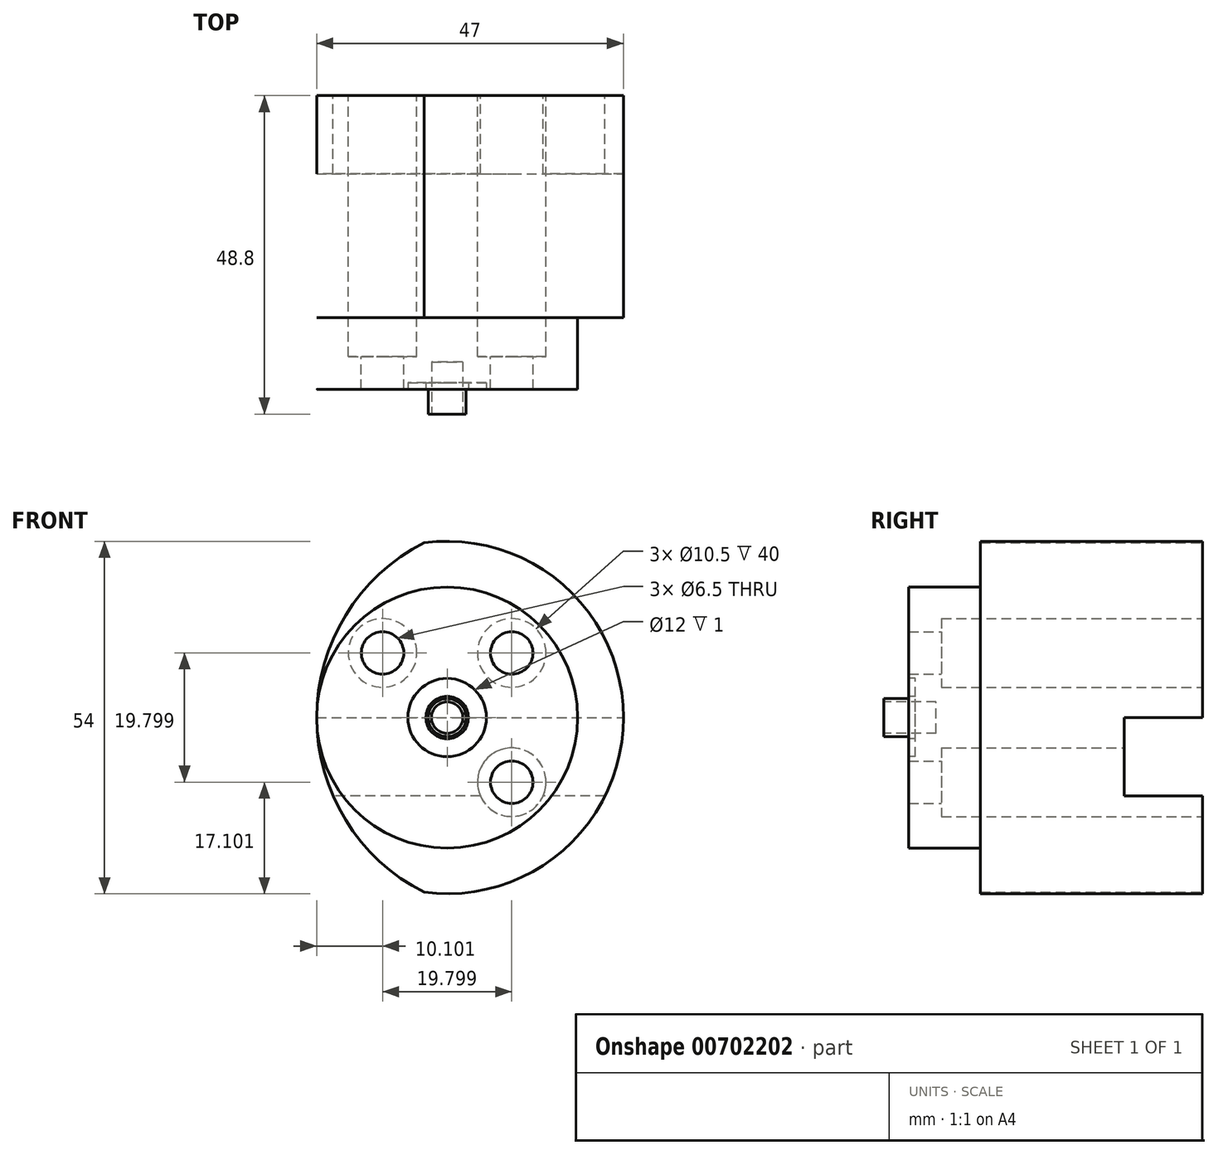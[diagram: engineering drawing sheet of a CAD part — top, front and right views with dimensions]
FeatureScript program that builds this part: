
annotation { "Feature Type Name" : "Feature", "Feature Type Description" : "" }
export const myFeature = defineFeature(function(context is Context, id is Id, definition is map)
    precondition{}
    {
        {
            var Q0;
            Q0=qCreatedBy(makeId("Front.planeOp"),FACE);
            var sketch = newSketch(context, id + "F0", { "sketchPlane" : qUnion([Q0])});
            skCircle(sketch, "E0", {"center": v(0, 0) * mm, "radius": 27 * mm});
            skSolve(sketch);
        }
        {
            var Q0;
            Q0 = qSketchRegion(id + "F0", true);
            extrude(context, id + "F1", {"entities" : qUnion([Q0]), "depth" : 45 * mm, "offsetDistance" : 25 * mm});
        }
        {
            var Q0;
            Q0=makeQuery(id+"F1.opExtrude","CAP_FACE",FACE,{"disambiguationData":[OSD([sQuery(id+"F0.wireOp",EDGE,"E0")])],"isStart":false});
            var sketch = newSketch(context, id + "F2", { "sketchPlane" : qUnion([Q0])});
            skCircle(sketch, "E1", {"center": v(0, 0) * mm, "radius": 20 * mm});
            skCircle(sketch, "E2", {"center": v(0, 0) * mm, "radius": 41.84 * mm});
            skSolve(sketch);
        }
        {
            var Q0;
            Q0 = qSketchRegion(id + "F2", true);
            extrude(context, id + "F3", {"entities" : qUnion([Q0]), "operationType" : NewBodyOperationType.REMOVE, "oppositeDirection" : true, "depth" : 11 * mm, "offsetDistance" : 25 * mm});
        }
        {
            var Q0;
            Q0=makeQuery(id+"F1.opExtrude","CAP_FACE",FACE,{"disambiguationData":[OSD([sQuery(id+"F0.wireOp",EDGE,"E0")])],"isStart":true});
            var sketch = newSketch(context, id + "F4", { "sketchPlane" : qUnion([Q0])});
            skPoint(sketch, "E3", {"position": v(9.9, 9.9) * mm});
            skLineSegment(sketch, "E4", {"start": v(9.9, 9.9) * mm, "end": v(0, 0) * mm});
            skLineSegment(sketch, "E5", {"start": v(0, 0) * mm, "end": v(47.47, 0) * mm});
            skLineSegment(sketch, "E6", {"start": v(0, 0) * mm, "end": v(0, 46.24) * mm});
            skPoint(sketch, "E7.MirrorP", {"position": v(-9.9, 9.9) * mm});
            skPoint(sketch, "E8.MirrorP", {"position": v(-9.9, -9.9) * mm});
            skSolve(sketch);
        }
        {
            var Q0;
            Q0=sQuery(id+"F4.wireOp",VERTEX,"E7.MirrorP");
            var Q1;
            Q1=sQuery(id+"F4.wireOp",VERTEX,"E3");
            var Q2;
            Q2=sQuery(id+"F4.wireOp",VERTEX,"42431aa4-3257-4c28-8b8a-731fc5cc6f3b0.MirrorP");
            var Q3;
            Q3=sQuery(id+"F4.wireOp",VERTEX,"E8.MirrorP");
            var Q4;
            Q4=makeQuery(id+"F1.opExtrude","SWEPT_BODY",BODY,{"disambiguationData":[OSD([sQuery(id+"F0.wireOp",EDGE,"E0")])]});
            hole(context, id + "F5", {"style" : HoleStyle.SIMPLE, "endStyle" : HoleEndStyle.BLIND, "holeDiameter" : 6.5 * mm, "majorDiameter" : 5 * mm, "holeDepth" : 50 * mm, "isTappedThrough" : true, "tappedDepth" : 12 * mm, "tapClearance" : 3, "locations" : qUnion([Q0, Q1, Q2, Q3]), "scope" : qUnion([Q4])});
        }
        {
            var Q0;
            Q0=makeQuery(id+"F1.opExtrude","CAP_FACE",FACE,{"disambiguationData":[OSD([sQuery(id+"F0.wireOp",EDGE,"E0")])],"isStart":true});
            var sketch = newSketch(context, id + "F6", { "sketchPlane" : qUnion([Q0])});
            skCircle(sketch, "E9", {"center": v(-9.9, -9.9) * mm, "radius": 5.25 * mm});
            skCircle(sketch, "E10", {"center": v(9.9, 9.9) * mm, "radius": 5.25 * mm});
            skCircle(sketch, "E11", {"center": v(-9.9, 9.9) * mm, "radius": 5.25 * mm});
            skSolve(sketch);
        }
        {
            var Q0;
            Q0 = qSketchRegion(id + "F6", true);
            extrude(context, id + "F7", {"entities" : qUnion([Q0]), "operationType" : NewBodyOperationType.REMOVE, "oppositeDirection" : true, "depth" : 40 * mm, "offsetDistance" : 25 * mm});
        }
        {
            var Q0;
            Q0=makeQuery(id+"F1.opExtrude","CAP_FACE",FACE,{"disambiguationData":[OSD([sQuery(id+"F0.wireOp",EDGE,"E0")])],"isStart":false});
            var sketch = newSketch(context, id + "F8", { "sketchPlane" : qUnion([Q0])});
            skCircle(sketch, "E12", {"center": v(0, 0) * mm, "radius": 2.9 * mm});
            skSolve(sketch);
        }
        {
            var Q0;
            Q0 = qSketchRegion(id + "F8", true);
            extrude(context, id + "F9", {"entities" : qUnion([Q0]), "operationType" : NewBodyOperationType.ADD, "depth" : 3.8 * mm, "offsetDistance" : 25 * mm});
        }
        {
            var Q0;
            Q0=makeQuery(id+"F9.opExtrude","CAP_FACE",FACE,{"disambiguationData":[OSD([sQuery(id+"F8.wireOp",EDGE,"E12")])],"isStart":false});
            var sketch = newSketch(context, id + "F10", { "sketchPlane" : qUnion([Q0])});
            skCircle(sketch, "E13", {"center": v(0, 0) * mm, "radius": 2.4 * mm});
            skSolve(sketch);
        }
        {
            var Q0;
            Q0 = qSketchRegion(id + "F10", true);
            extrude(context, id + "F11", {"entities" : qUnion([Q0]), "operationType" : NewBodyOperationType.REMOVE, "oppositeDirection" : true, "depth" : 8 * mm, "offsetDistance" : 25 * mm});
        }
        {
            var Q0;
            Q0=makeQuery(id+"F1.opExtrude","CAP_FACE",FACE,{"disambiguationData":[OSD([sQuery(id+"F0.wireOp",EDGE,"E0")])],"isStart":false});
            var sketch = newSketch(context, id + "F12", { "sketchPlane" : qUnion([Q0])});
            skCircle(sketch, "E14", {"center": v(0, 0) * mm, "radius": 6 * mm});
            skCircle(sketch, "E15", {"center": v(0, 0) * mm, "radius": 3.25 * mm});
            skSolve(sketch);
        }
        {
            var Q0;
            Q0 = qSketchRegion(id + "F12", true);
            extrude(context, id + "F13", {"entities" : qUnion([Q0]), "operationType" : NewBodyOperationType.REMOVE, "oppositeDirection" : true, "depth" : 1 * mm, "offsetDistance" : 25 * mm});
        }
        {
            var Q0;
            Q0=makeQuery(id+"F1.opExtrude","CAP_FACE",FACE,{"disambiguationData":[OSD([sQuery(id+"F0.wireOp",EDGE,"E0")])],"isStart":true});
            var sketch = newSketch(context, id + "F14", { "sketchPlane" : qUnion([Q0])});
            skLineSegment(sketch, "E16", {"start": v(0, 0) * mm, "end": v(-37.34, 0) * mm});
            skLineSegment(sketch, "E17", {"start": v(-37.34, 0) * mm, "end": v(-37.34, -12) * mm});
            skLineSegment(sketch, "E18", {"start": v(-37.34, -12) * mm, "end": v(41.68, -12) * mm});
            skLineSegment(sketch, "E19", {"start": v(41.68, -12) * mm, "end": v(39.8, 0) * mm});
            skLineSegment(sketch, "E20", {"start": v(39.8, 0) * mm, "end": v(0, 0) * mm});
            skSolve(sketch);
        }
        {
            var Q0;
            Q0 = qSketchRegion(id + "F14", true);
            extrude(context, id + "F15", {"entities" : qUnion([Q0]), "operationType" : NewBodyOperationType.REMOVE, "oppositeDirection" : true, "depth" : 12 * mm, "offsetDistance" : 25 * mm});
        }
        {
            var Q0;
            {var subQ0=sQuery(id+"F0.wireOp",EDGE,"E0");Q0=makeQuery(id+"F15.boolean.opBoolean","SPLIT",FACE,{"disambiguationData":[TD([makeQuery(id+"F7.boolean.opBoolean","COPY",FACE,{"derivedFrom":makeQuery(id+"F7.opExtrude","SWEPT_FACE",FACE,{"disambiguationData":[OSD([sQuery(id+"F6.wireOp",EDGE,"E10")])]})})])],"derivedFrom":makeQuery(id+"F1.opExtrude","CAP_FACE",FACE,{"disambiguationData":[OSD([subQ0])],"isStart":true})});}
            var sketch = newSketch(context, id + "F16", { "sketchPlane" : qUnion([Q0])});
            skPoint(sketch, "E21", {"position": v(20, 0) * mm});
            skPoint(sketch, "E22", {"position": v(27, 0) * mm});
            skPoint(sketch, "E23", {"position": v(-10, 0) * mm});
            skCircle(sketch, "E24", {"center": v(-10, 0) * mm, "radius": 30 * mm});
            skCircle(sketch, "E25", {"center": v(-10, 0) * mm, "radius": 45.27 * mm});
            skPoint(sketch, "E26", {"position": v(42, 0) * mm});
            skSolve(sketch);
        }
        {
            var Q0;
            Q0 = qSketchRegion(id + "F16", true);
            extrude(context, id + "F17", {"entities" : qUnion([Q0]), "operationType" : NewBodyOperationType.REMOVE, "oppositeDirection" : true, "depth" : 53.4 * mm, "offsetDistance" : 25 * mm});
        }
    });
